# Revit family: LCL
name_source: partatom
category: Lighting Fixtures
units: mm (PartAtom-declared; Revit-internal decimal feet)

## family parameters
Cut with Voids When Loaded = No
Host = Face
Light Source = Yes
OmniClass Number = 23.80.70.11
OmniClass Title = Luminaries for Internal Lighting
Part Type = Normal
Room Calculation Point = No
Round Connector Dimension = Use Diameter
Shared = No

## types (2) — shared parameters
Apparent Load = 0 VA
Backbox = White
Color Filter = 16777215
Default Elevation = 48"
Description = Columbia's LCL is an LED striplight with a formed acrylic lens to eliminate pixilation and reduce glare.
Dimming Lamp Color Temperature Shift = <None>
Emit Shape Visible in Rendering = No
Emit from Rectangle Length = 47 1/2"
Emit from Rectangle Width = 4 1/4"
Glass = White Glass
Lamp = LED Lamp
Manufacturer = Columbia Lighting
Model = LCL
Row Length = 48"
Tilt Angle = -90.00°
Voltage = 120 V
Wattage Comments = Up to 110 lumens per watt

## per-type parameters (varying)
| type | Lumen Output | Nominal Watts | Photometric Web File | Product Documentation Link | Product Page URL | URL |
| LCL4-40ML-EDU | Medium Lumen | 48 W | LCL4-40ML-EDU.ies | http://www.columbialighting.com | http://www.columbialighting.com | http://www.columbialighting.com |
| LCL4-40VL-EDU | Very High Lumen | 96 W | LCL4-40VL-EDU.ies |  |  | https://www.currentlighting.com |

## geometry (parser evidence)
native form markers: Sweep x4
no freeform markers — native parametric forms only
